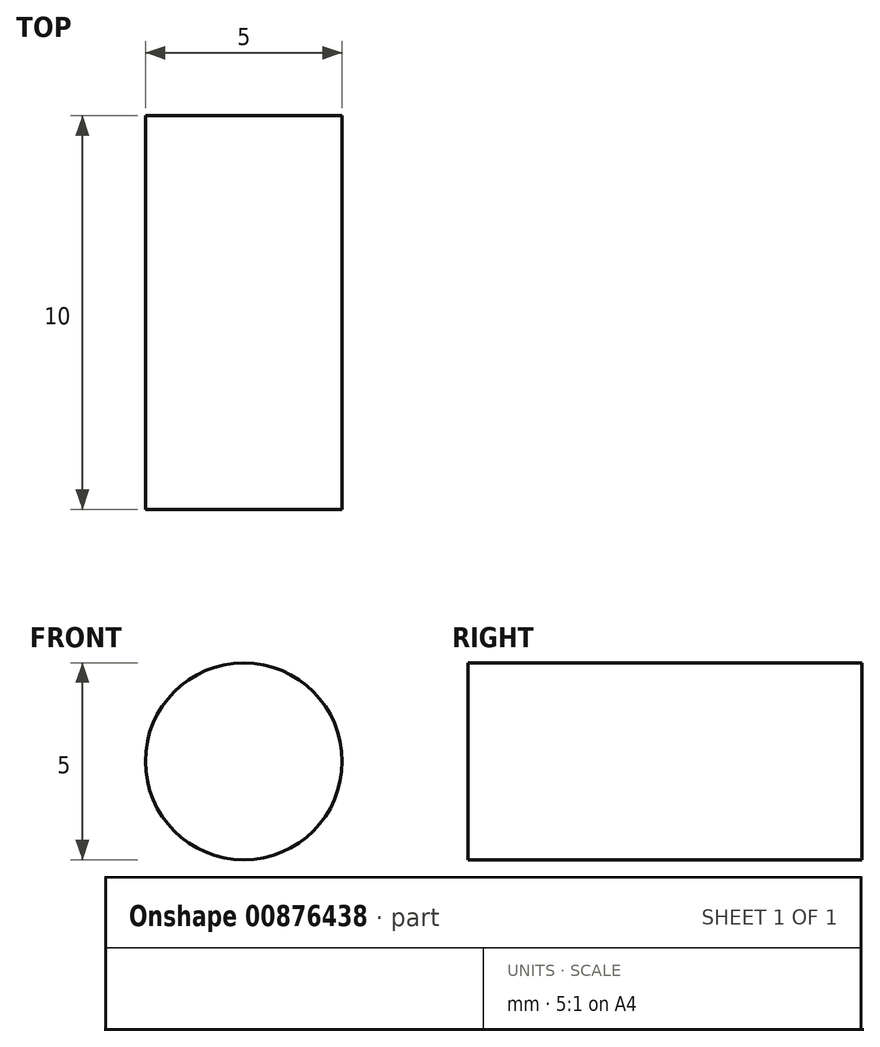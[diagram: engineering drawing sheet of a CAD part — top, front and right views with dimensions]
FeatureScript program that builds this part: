
annotation { "Feature Type Name" : "Feature", "Feature Type Description" : "" }
export const myFeature = defineFeature(function(context is Context, id is Id, definition is map)
    precondition{}
    {
        {
            var Q0;
            Q0=qCreatedBy(makeId("Front.planeOp"),FACE);
            var sketch = newSketch(context, id + "F0", { "sketchPlane" : qUnion([Q0])});
            skCircle(sketch, "E0", {"center": v(0, 0) * mm, "radius": 2.5 * mm});
            skSolve(sketch);
        }
        {
            var Q0;
            Q0 = qSketchRegion(id + "F0", true);
            extrude(context, id + "F1", {"entities" : qUnion([Q0]), "endBound" : BoundingType.SYMMETRIC, "oppositeDirection" : true, "depth" : 10 * mm, "offsetDistance" : 25 * mm});
        }
    });
